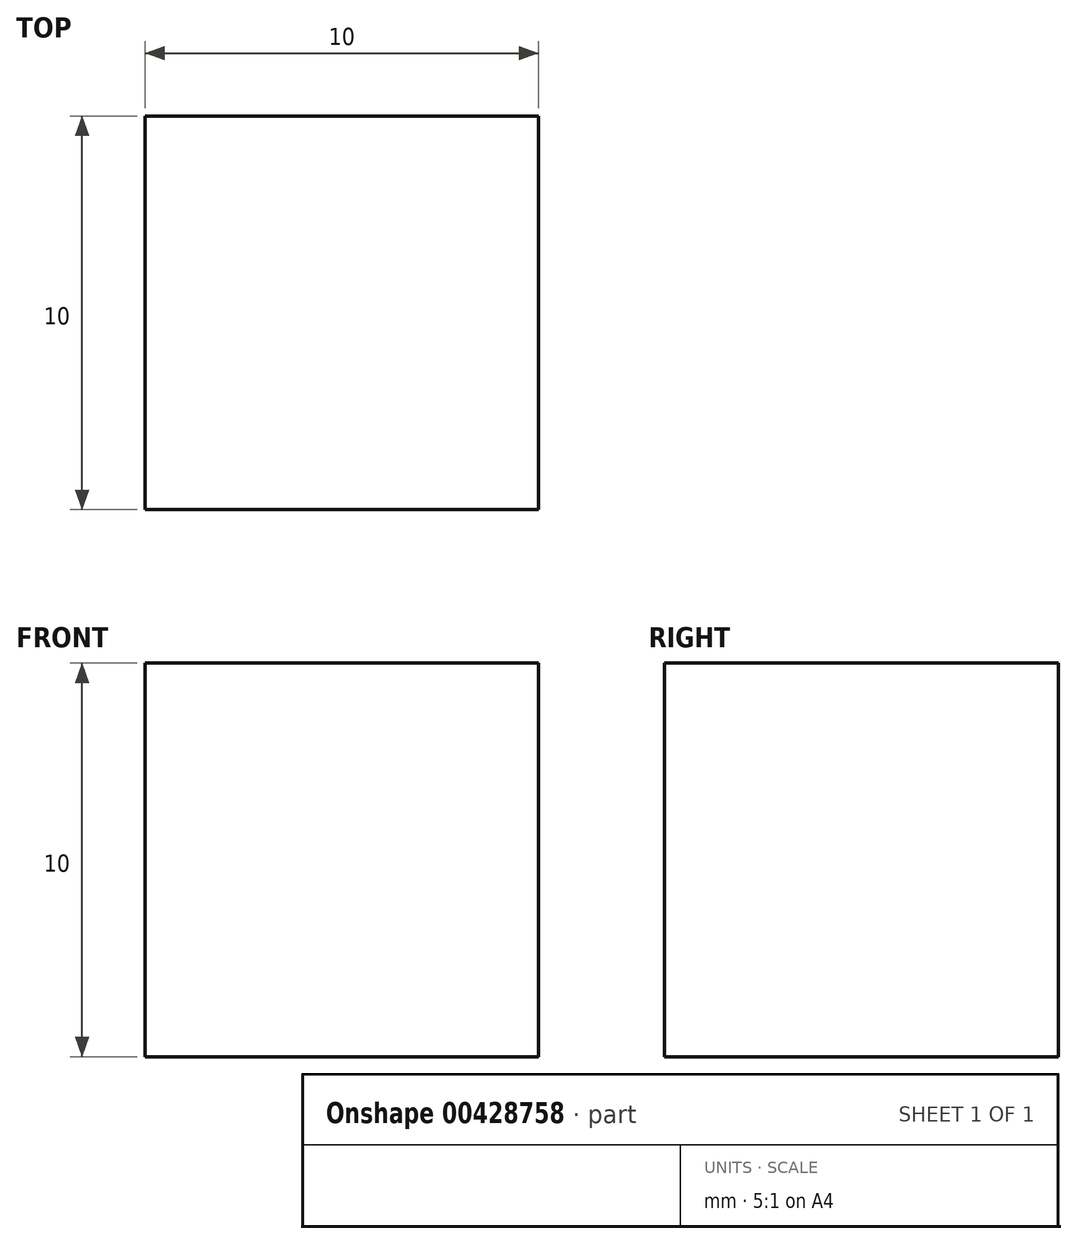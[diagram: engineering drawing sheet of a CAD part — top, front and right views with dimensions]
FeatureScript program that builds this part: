
annotation { "Feature Type Name" : "Feature", "Feature Type Description" : "" }
export const myFeature = defineFeature(function(context is Context, id is Id, definition is map)
    precondition{}
    {
        {
            var Q0;
            Q0=qCreatedBy(makeId("Front.planeOp"),FACE);
            var sketch = newSketch(context, id + "F0", { "sketchPlane" : qUnion([Q0])});
            skLineSegment(sketch, "E0.bottom", {"start": v(-5, 5) * mm, "end": v(5, 5) * mm});
            skLineSegment(sketch, "E0.top", {"start": v(-5, -5) * mm, "end": v(5, -5) * mm});
            skLineSegment(sketch, "E0.left", {"start": v(-5, 5) * mm, "end": v(-5, -5) * mm});
            skLineSegment(sketch, "E0.right", {"start": v(5, 5) * mm, "end": v(5, -5) * mm});
            skPoint(sketch, "E0.middle", {"position": v(0, 0) * mm});
            skSolve(sketch);
        }
        {
            var Q0;
            Q0=makeQuery(id+"F0.imprint","IMPRINT",FACE,{"disambiguationData":[TD([[makeQuery(id+"F0.imprint","IMPRINT",EDGE,{"derivedFrom":sQuery(id+"F0.wireOp",EDGE,"E0.bottom")}),-1.0]])]});
            extrude(context, id + "F1", {"entities" : qUnion([Q0]), "depth" : 10 * mm});
        }
    });
